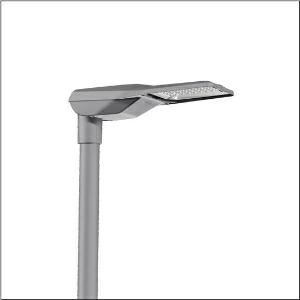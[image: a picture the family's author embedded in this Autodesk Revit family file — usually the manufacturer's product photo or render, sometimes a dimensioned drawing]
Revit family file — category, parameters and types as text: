
# Revit family: streetlight_sl_21_iq_mini___st0_8a_5xe2c31g08hb_2845
name_source: partatom
category: Lighting Fixtures
units: mm (PartAtom-declared; Revit-internal decimal feet)

## family parameters
Cut with Voids When Loaded = No
Host = Face
Light Source = No
Part Type = Normal
Room Calculation Point = No
Round Connector Dimension = Use Diameter
Shared = No

## types (1)
- --- (1 x LED, 9450 lm, 70.9 W, 3000K)
    Apparent Load = 71 VA
    CIE Flux Codes = 38 75 97 100 100
    Color Rendering = 70
    Color Temperature = 3000K
    Default Elevation = 1800 mm
    Description = Streetlight SL 21 iQ mini, mast luminaire, primary light control with lens, of PMMA, primary optical cover: cover, of toughened safety glass, transparent, light distribution: ST0.8a, light emission: direct distribution, primary light characteristic: asymmetric, installation type: post-top, side-entry, LED, High Power LED, rated luminous flux: 9.450lm, luminous efficacy: 133lm/W, light colour: 730, colour temperature: 3000K, control: Street-Remote, Auto-Match, Temp-Guard, Lumen-Switch, Night-Set, Smart-Wire, Light-Fading, Desk-Remote (wireless, voltage-free reading and setting of iQ features in the workshop via application-optimized NFC function/RFID function), optimised constant luminous flux control (CLO 2.0), pre-setting: linear dimming characteristic, mains connection: 220..240V, AC, 50/60Hz, start of lifetime: 71W, end of service life: 75W, reduction: 31W, luminaire housing, of diecast aluminium, powder-coated, Siteco® metallic grey (DB 702S), corrosivity category C5 mid according to DIN EN ISO 12944, please order mast flange separately, inclination adjustable: 0°, 5°, 10°, 15°, sealing non-destructively replaceable, multi-level sealing system, length: 628mm, width: 235mm, height: 110mm, mast flange for spigot size: 42mm (side-entry): 5XC10008XM4, 60/48mm (side-entry/post-top): 5XC10108XM2, 76/60mm (side-entry/post-top): 5XC10108XM1, protection rating (complete): IP66, insulation class (complete): insulation class II (safety insulation), certification: CE, ENEC, ENEC+, VDE, impact resistance: IK09, permissible operating ambient temperature for outdoor applications: -40..+50°C, standard-compliant lighting for roads and squares, packaging unit: 1 piece

Light Distribution: ST0.8a
    Height = 110 mm
    Lamp = 1 x LED
    Lamp Light Flux = 9450 lm
    Lamp Power = 70.9 W
    Lamp count = 1
    Length = 625 mm
    Luminous efficacy = 133 lm/W
    Manufacturer = Siteco
    ModVariant = No
    Model = 5XE2C31G08HB
    Number of Poles = 1
    OnlyDefault = Yes
    Power Factor = 1
    Product Name = Streetlight SL 21 iQ mini | ST0.8a
    Product group = mast luminaire | pylon top
    ProductGroupID = 6100
    Protection Class = Protection class II
    Protection Degree = IP 66
    RLX_Detail_Level = 1
    RLX_Emergency_Light_Flux = 0 lm
    RLX_Emergency_Type = 0
    RLX_Emergency_Type_DB = No
    RlxData = <blob elided: 92641 chars, md5=58390b64>
    Socket = socket
    Standby Power = 0 W
    System Light Flux = 9450 lm
    System Power = 71 W
    Type Comments = factory setting: luminous flux: 100 % | dim-lin: 254 | 711 mA
    Type Image = l_1003519.jpg
    URL = http://relux.com
    VarID = @adj_127761
    Voltage = 0 V
    Weight = 0.00 kg
    Width = 234 mm

## geometry (parser evidence)
native form markers: Blend x4, Sweep x12
no freeform markers — native parametric forms only
